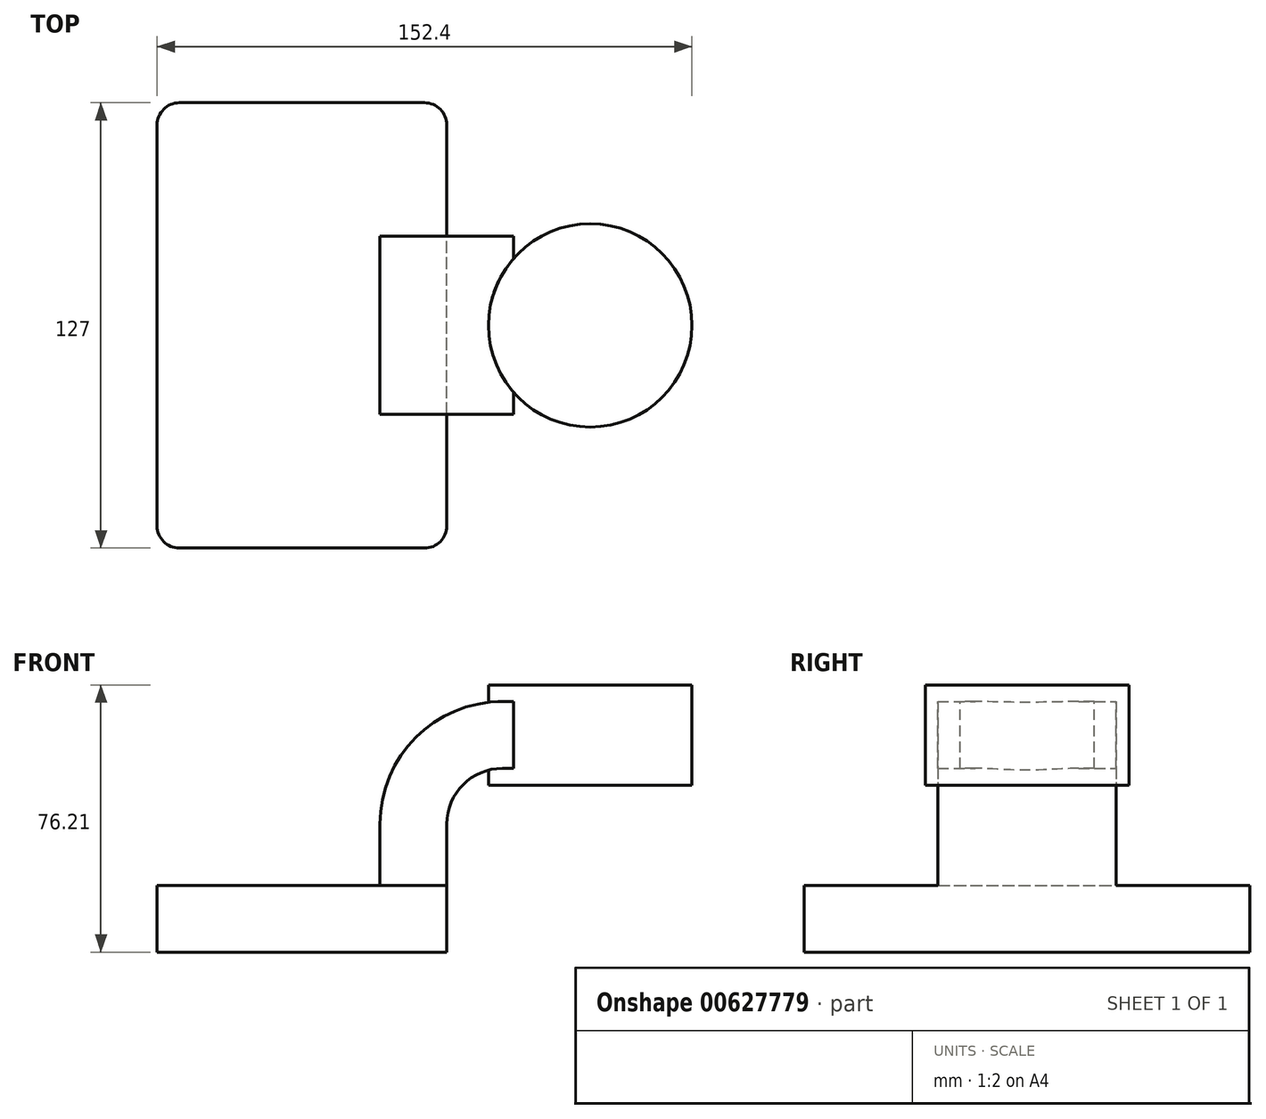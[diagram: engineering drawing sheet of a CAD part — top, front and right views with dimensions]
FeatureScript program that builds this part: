
annotation { "Feature Type Name" : "Feature", "Feature Type Description" : "" }
export const myFeature = defineFeature(function(context is Context, id is Id, definition is map)
    precondition{}
    {
        {
            var Q0;
            Q0=qCreatedBy(makeId("Front.planeOp"),FACE);
            var sketch = newSketch(context, id + "F0", { "sketchPlane" : qUnion([Q0])});
            skLineSegment(sketch, "E0.bottom", {"start": v(-41.28, -9.53) * mm, "end": v(41.28, -9.53) * mm});
            skLineSegment(sketch, "E0.top", {"start": v(-41.28, 9.53) * mm, "end": v(41.28, 9.53) * mm});
            skLineSegment(sketch, "E0.left", {"start": v(-41.28, -9.53) * mm, "end": v(-41.28, 9.53) * mm});
            skLineSegment(sketch, "E0.right", {"start": v(41.28, -9.53) * mm, "end": v(41.28, 9.53) * mm});
            skPoint(sketch, "E0.middle", {"position": v(0, 0) * mm});
            skLineSegment(sketch, "E1.bottom", {"start": v(111.12, 38.1) * mm, "end": v(60.33, 38.1) * mm});
            skLineSegment(sketch, "E1.top", {"start": v(111.12, 66.68) * mm, "end": v(60.32, 66.67) * mm});
            skLineSegment(sketch, "E1.left", {"start": v(111.12, 38.1) * mm, "end": v(111.12, 66.68) * mm});
            skLineSegment(sketch, "E1.right", {"start": v(60.33, 38.1) * mm, "end": v(60.32, 66.67) * mm});
            skPoint(sketch, "E1.middle", {"position": v(85.72, 52.39) * mm});
            skLineSegment(sketch, "E2", {"start": v(41.27, 9.52) * mm, "end": v(41.27, 27) * mm});
            skArc(sketch, "E3", {"start": v(41.27, 27) * mm, "mid": v(45.92, 38.23) * mm, "end": v(57.15, 42.88) * mm});
            skLineSegment(sketch, "E4", {"start": v(57.15, 42.88) * mm, "end": v(82.13, 42.88) * mm});
            skLineSegment(sketch, "E5.0", {"start": v(57.15, 61.93) * mm, "end": v(82.13, 61.93) * mm});
            skArc(sketch, "E5.1", {"start": v(22.22, 27) * mm, "mid": v(32.45, 51.7) * mm, "end": v(57.15, 61.93) * mm});
            skLineSegment(sketch, "E5.2", {"start": v(22.23, 9.52) * mm, "end": v(22.23, 27) * mm});
            skLineSegment(sketch, "E6", {"start": v(82.13, 66.67) * mm, "end": v(82.13, 38.1) * mm});
            skFitSpline(sketch, "E7", {"points": [v(-41.28, 9.53) * mm, v(57.15, 61.93) * mm], "startDerivative": vector(30, 127.28) * mm, "endDerivative": vector(112.03, -2.83) * mm});
            skSolve(sketch);
        }
        {
            var Q0;
            Q0=makeQuery(id+"F0.imprint","IMPRINT",FACE,{"disambiguationData":[TD([[makeQuery(id+"F0.imprint","IMPRINT",EDGE,{"derivedFrom":sQuery(id+"F0.wireOp",EDGE,"E0.bottom")}),1.0]])]});
            extrude(context, id + "F1", {"entities" : qUnion([Q0]), "endBound" : BoundingType.SYMMETRIC, "depth" : 127 * mm, "offsetDistance" : 25.4 * mm});
        }
        {
            var Q0;
            {var subQ1=sQuery(id+"F0.wireOp",EDGE,"E2");Q0=makeQuery(id+"F0.imprint","IMPRINT",FACE,{"disambiguationData":[TD([[makeQuery(id+"F0.imprint","IMPRINT",EDGE,{"derivedFrom":subQ1}),1.0]])]});}
            extrude(context, id + "F2", {"entities" : qUnion([Q0]), "operationType" : NewBodyOperationType.ADD, "endBound" : BoundingType.SYMMETRIC, "depth" : 50.8 * mm, "offsetDistance" : 25.4 * mm});
        }
        {
            var Q0;
            Q0=makeQuery(id+"F0.imprint","IMPRINT",FACE,{"disambiguationData":[TD([[makeQuery(id+"F0.imprint","IMPRINT",EDGE,{"derivedFrom":sQuery(id+"F0.wireOp",EDGE,"E5.1")}),1.0]])]});
            extrude(context, id + "F3", {"entities" : qUnion([Q0]), "operationType" : NewBodyOperationType.ADD, "endBound" : BoundingType.SYMMETRIC, "depth" : 15.88 * mm, "offsetDistance" : 25.4 * mm});
        }
        {
            var Q0;
            {var subQ4=sQuery(id+"F0.wireOp",EDGE,"E1.left");Q0=makeQuery(id+"F0.imprint","IMPRINT",FACE,{"disambiguationData":[TD([[makeQuery(id+"F0.imprint","IMPRINT",EDGE,{"derivedFrom":subQ4}),1.0]])]});}
            var Q1;
            Q1=sQuery(id+"F0.wireOp",EDGE,"E6");
            revolve(context, id + "F4", {"operationType" : NewBodyOperationType.ADD, "entities" : qUnion([Q0]), "axis" : qUnion([Q1]), "revolveType" : RevolveType.FULL});
        }
        {
            var Q0;
            Q0=makeQuery(id+"F1.opExtrude","CAP_EDGE",EDGE,{"disambiguationData":[OSD([sQuery(id+"F0.wireOp",EDGE,"E0.right")])],"isStart":false});
            var Q1;
            Q1=makeQuery(id+"F1.opExtrude","CAP_EDGE",EDGE,{"disambiguationData":[OSD([sQuery(id+"F0.wireOp",EDGE,"E0.left")])],"isStart":false});
            var Q2;
            Q2=makeQuery(id+"F1.opExtrude","CAP_EDGE",EDGE,{"disambiguationData":[OSD([sQuery(id+"F0.wireOp",EDGE,"E0.right")])],"isStart":true});
            var Q3;
            Q3=makeQuery(id+"F1.opExtrude","CAP_EDGE",EDGE,{"disambiguationData":[OSD([sQuery(id+"F0.wireOp",EDGE,"E0.left")])],"isStart":true});
            fillet(context, id + "F5", {"entities" : qUnion([Q0, Q1, Q2, Q3]), "radius" : 6.35 * mm, "tangentPropagation" : true, "allowEdgeOverflow" : false});
        }
    });
